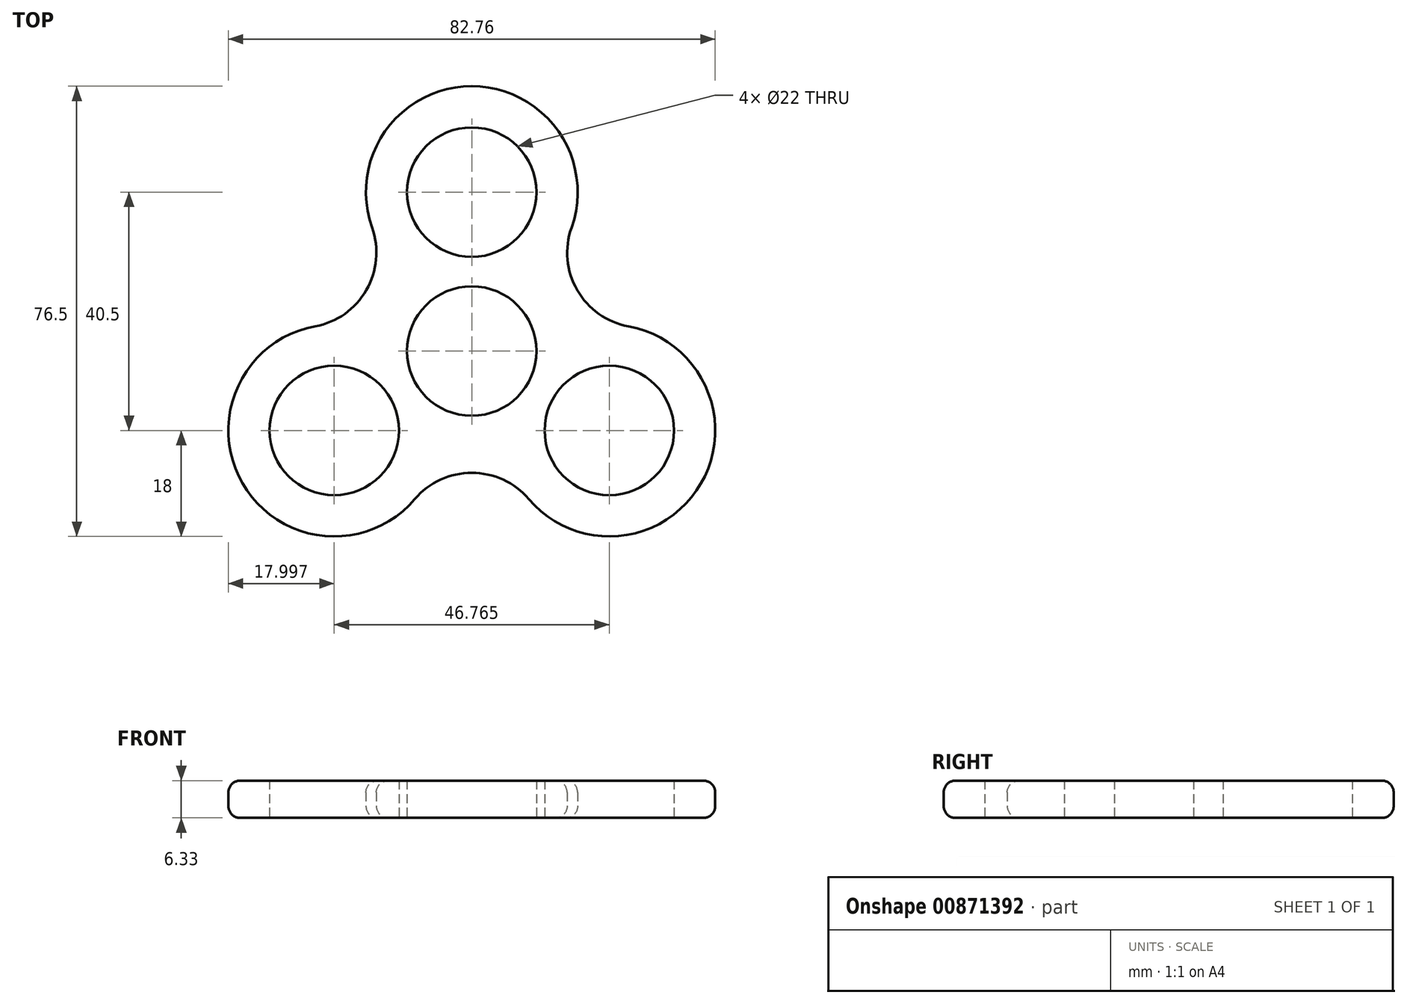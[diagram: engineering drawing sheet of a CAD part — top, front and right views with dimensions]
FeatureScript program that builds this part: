
annotation { "Feature Type Name" : "Feature", "Feature Type Description" : "" }
export const myFeature = defineFeature(function(context is Context, id is Id, definition is map)
    precondition{}
    {
        {
            var Q0;
            Q0=qCreatedBy(makeId("Top.planeOp"),FACE);
            var sketch = newSketch(context, id + "F0", { "sketchPlane" : qUnion([Q0])});
            skLineSegment(sketch, "E0", {"start": v(0, 0) * mm, "end": v(0, 27) * mm, "construction": true});
            skLineSegment(sketch, "E1", {"start": v(0, 0) * mm, "end": v(23.38, -13.5) * mm, "construction": true});
            skLineSegment(sketch, "E2", {"start": v(0, 0) * mm, "end": v(-23.38, -13.5) * mm, "construction": true});
            skCircle(sketch, "E3", {"center": v(0, 0) * mm, "radius": 27 * mm, "construction": true});
            skCircle(sketch, "E4", {"center": v(23.38, -13.5) * mm, "radius": 11 * mm});
            skCircle(sketch, "E5", {"center": v(-23.38, -13.5) * mm, "radius": 11 * mm});
            skCircle(sketch, "E6", {"center": v(0, 27) * mm, "radius": 11 * mm});
            skCircle(sketch, "E7", {"center": v(0, 0) * mm, "radius": 11 * mm});
            skCircle(sketch, "E8", {"center": v(0, 27) * mm, "radius": 18 * mm});
            skCircle(sketch, "E9", {"center": v(-23.38, -13.5) * mm, "radius": 18 * mm});
            skCircle(sketch, "E10", {"center": v(23.38, -13.5) * mm, "radius": 18 * mm});
            skCircle(sketch, "E11", {"center": v(-28.92, 16.7) * mm, "radius": 12.7 * mm});
            skCircle(sketch, "E12", {"center": v(0, -33.4) * mm, "radius": 12.7 * mm});
            skCircle(sketch, "E13", {"center": v(28.92, 16.7) * mm, "radius": 12.7 * mm});
            skSolve(sketch);
        }
        {
            var Q0;
            Q0=qCreatedBy(makeId("Top.planeOp"),FACE);
            var sketch = newSketch(context, id + "F1", { "sketchPlane" : qUnion([Q0])});
            skArc(sketch, "E14.0", {"start": v(16.96, 20.96) * mm, "mid": v(0, 45) * mm, "end": v(-16.96, 20.96) * mm});
            skArc(sketch, "E14.1", {"start": v(-26.63, 4.2) * mm, "mid": v(-17.92, 10.35) * mm, "end": v(-16.96, 20.96) * mm});
            skArc(sketch, "E14.2", {"start": v(-26.63, 4.2) * mm, "mid": v(-38.97, -22.5) * mm, "end": v(-9.67, -25.16) * mm});
            skArc(sketch, "E14.3", {"start": v(9.67, -25.16) * mm, "mid": v(0, -20.7) * mm, "end": v(-9.67, -25.16) * mm});
            skArc(sketch, "E14.4", {"start": v(9.67, -25.16) * mm, "mid": v(38.97, -22.5) * mm, "end": v(26.63, 4.2) * mm});
            skArc(sketch, "E14.5", {"start": v(16.96, 20.96) * mm, "mid": v(17.92, 10.35) * mm, "end": v(26.63, 4.2) * mm});
            skSolve(sketch);
        }
        {
            var Q0;
            Q0=qSketchRegion(id+"F1",true);
            extrude(context, id + "F2", {"entities" : qUnion([Q0]), "depth" : 6.33 * mm, "offsetDistance" : 25 * mm});
        }
        {
            var Q0;
            Q0=qCreatedBy(makeId("Top.planeOp"),FACE);
            var sketch = newSketch(context, id + "F3", { "sketchPlane" : qUnion([Q0])});
            skCircle(sketch, "E15.0", {"center": v(-23.38, -13.5) * mm, "radius": 11 * mm});
            skCircle(sketch, "E15.1", {"center": v(0, 27) * mm, "radius": 11 * mm});
            skCircle(sketch, "E15.2", {"center": v(23.38, -13.5) * mm, "radius": 11 * mm});
            skCircle(sketch, "E15.3", {"center": v(0, 0) * mm, "radius": 11 * mm});
            skSolve(sketch);
        }
        {
            var Q0;
            Q0=qSketchRegion(id+"F3",true);
            extrude(context, id + "F4", {"entities" : qUnion([Q0]), "operationType" : NewBodyOperationType.REMOVE, "endBound" : BoundingType.THROUGH_ALL, "depth" : 25 * mm, "offsetDistance" : 25 * mm});
        }
        {
            var Q0;
            Q0=makeQuery(id+"F2.opExtrude","CAP_EDGE",EDGE,{"disambiguationData":[OSD([sQuery(id+"F1.wireOp",EDGE,"E14.0")])],"isStart":false});
            var Q1;
            Q1=makeQuery(id+"F2.opExtrude","CAP_EDGE",EDGE,{"disambiguationData":[OSD([sQuery(id+"F1.wireOp",EDGE,"E14.1")])],"isStart":false});
            var Q2;
            Q2=makeQuery(id+"F2.opExtrude","CAP_EDGE",EDGE,{"disambiguationData":[OSD([sQuery(id+"F1.wireOp",EDGE,"E14.2")])],"isStart":true});
            fillet(context, id + "F5", {"entities" : qUnion([Q0, Q1, Q2]), "radius" : 2 * mm, "tangentPropagation" : true, "allowEdgeOverflow" : false});
        }
    });
